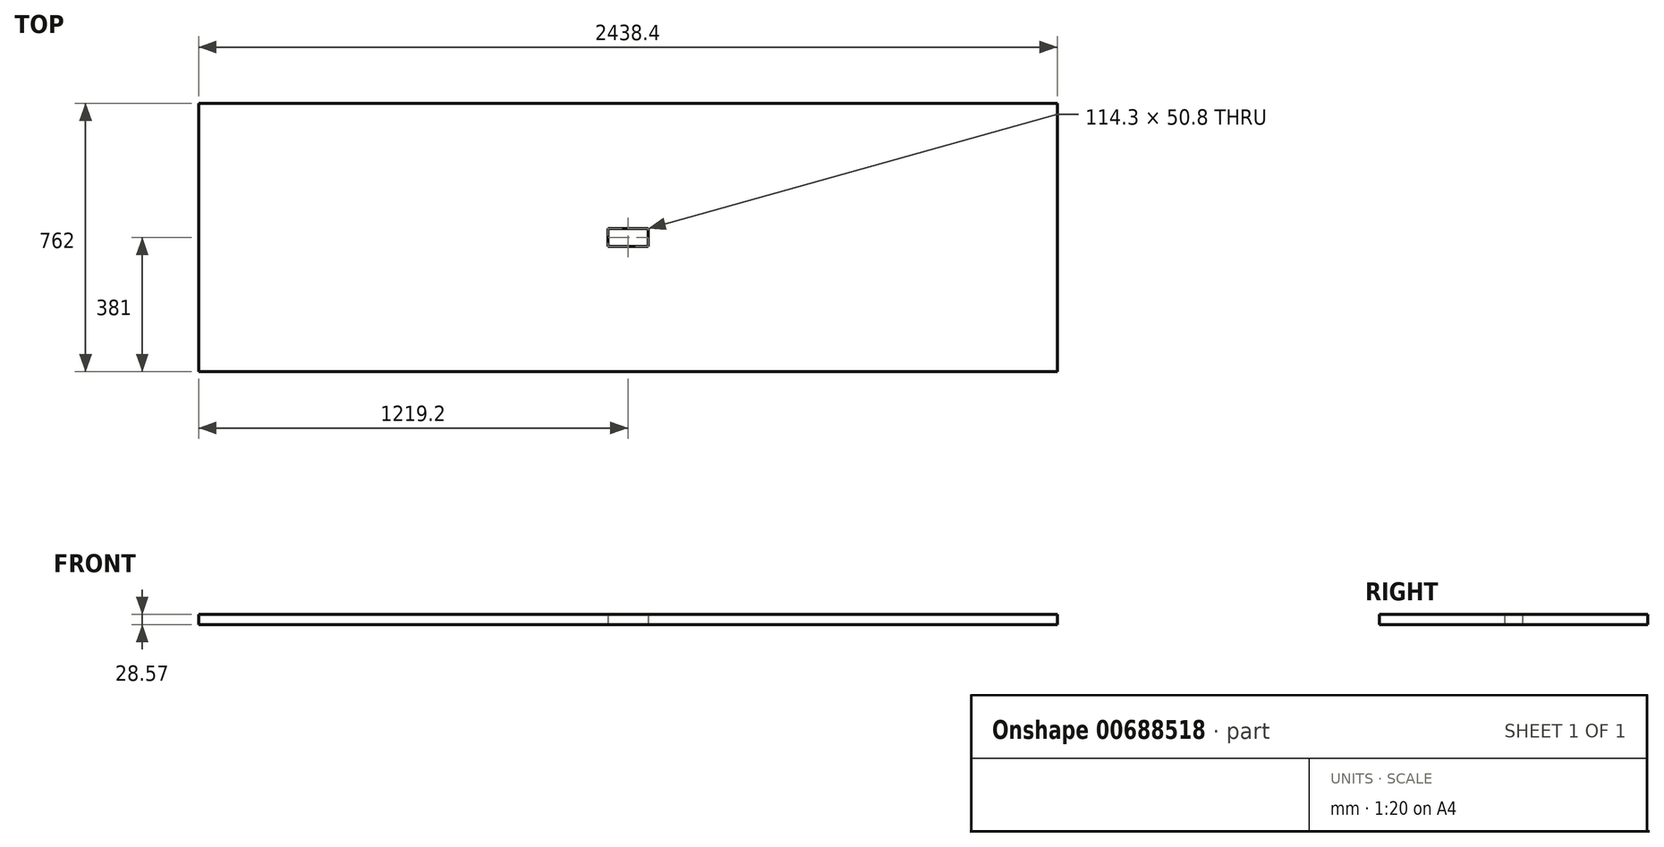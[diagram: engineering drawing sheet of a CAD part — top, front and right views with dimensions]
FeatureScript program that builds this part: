
annotation { "Feature Type Name" : "Feature", "Feature Type Description" : "" }
export const myFeature = defineFeature(function(context is Context, id is Id, definition is map)
    precondition{}
    {
        {
            var Q0;
            Q0=qCreatedBy(makeId("Top.planeOp"),FACE);
            var sketch = newSketch(context, id + "F0", { "sketchPlane" : qUnion([Q0])});
            skLineSegment(sketch, "E0.bottom", {"start": v(1219.2, 381) * mm, "end": v(-1219.2, 381) * mm});
            skLineSegment(sketch, "E0.top", {"start": v(1219.2, -381) * mm, "end": v(-1219.2, -381) * mm});
            skLineSegment(sketch, "E0.left", {"start": v(1219.2, 381) * mm, "end": v(1219.2, -381) * mm});
            skLineSegment(sketch, "E0.right", {"start": v(-1219.2, 381) * mm, "end": v(-1219.2, -381) * mm});
            skPoint(sketch, "E0.middle", {"position": v(0, 0) * mm});
            skLineSegment(sketch, "E1.bottom", {"start": v(57.15, 25.4) * mm, "end": v(-57.15, 25.4) * mm});
            skLineSegment(sketch, "E1.top", {"start": v(57.15, -25.4) * mm, "end": v(-57.15, -25.4) * mm});
            skLineSegment(sketch, "E1.left", {"start": v(57.15, 25.4) * mm, "end": v(57.15, -25.4) * mm});
            skLineSegment(sketch, "E1.right", {"start": v(-57.15, 25.4) * mm, "end": v(-57.15, -25.4) * mm});
            skSolve(sketch);
        }
        {
            var Q0;
            Q0=makeQuery(id+"F0.imprint","IMPRINT",FACE,{"disambiguationData":[TD([[makeQuery(id+"F0.imprint","IMPRINT",EDGE,{"derivedFrom":sQuery(id+"F0.wireOp",EDGE,"E0.bottom")}),1.0]])]});
            extrude(context, id + "F1", {"entities" : qUnion([Q0]), "depth" : 28.57 * mm, "offsetDistance" : 25.4 * mm});
        }
    });
